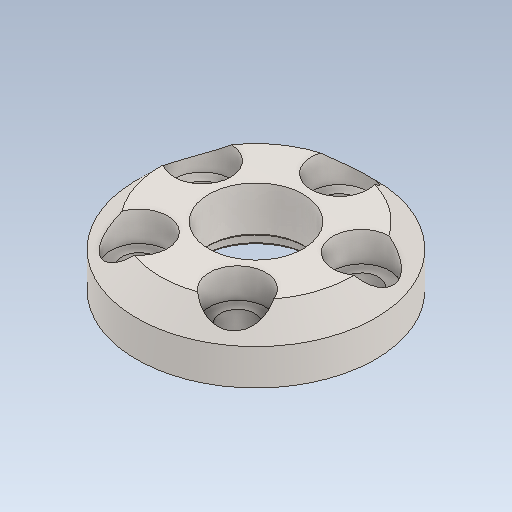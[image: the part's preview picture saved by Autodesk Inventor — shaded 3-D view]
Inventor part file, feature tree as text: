
AUTODESK INVENTOR PART (.ipt)
format: ipt  version: 2020 (Build 240168000, 168)  size: 173,056 bytes
history: native  units: in
note: dims shown in document units (in); Inventor stores cm internally (conversion verified against a paired STEP export)
features: chamfer x1
ambient origin geometry x8: Origin, YZ Plane, XZ Plane, XY Plane, X Axis, Y Axis, Z Axis, Center Point
bodies: Solid1 (feature_tree)
feature tree (1):
  chamfer  "Chamfer2"  [1 undecoded]
note: 1 required parameter value undecoded (feature->parameter linkage not recoverable at this tier; creation-order binding heuristic only, values carry confidence <= 0.55)
